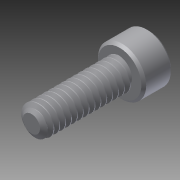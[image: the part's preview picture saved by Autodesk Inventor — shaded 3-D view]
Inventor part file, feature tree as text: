
AUTODESK INVENTOR PART (.ipt)
format: ipt  version: 2015 (Build 190159000, 159)  size: 588,800 bytes
history: native  units: in
note: dims shown in document units (in); Inventor stores cm internally (conversion verified against a paired STEP export)
features: chamfer x1, other x1, imported_body x1
ambient origin geometry x8: Origin, YZ Plane, XZ Plane, XY Plane, X Axis, Y Axis, Z Axis, Center Point
bodies: Body1 (feature_tree)
feature tree (3):
  chamfer  "Chamfer1"  [1 undecoded]
  other  "92185A1341"
  imported_body  "Base1"
note: 1 required parameter value undecoded (feature->parameter linkage not recoverable at this tier; creation-order binding heuristic only, values carry confidence <= 0.55)
